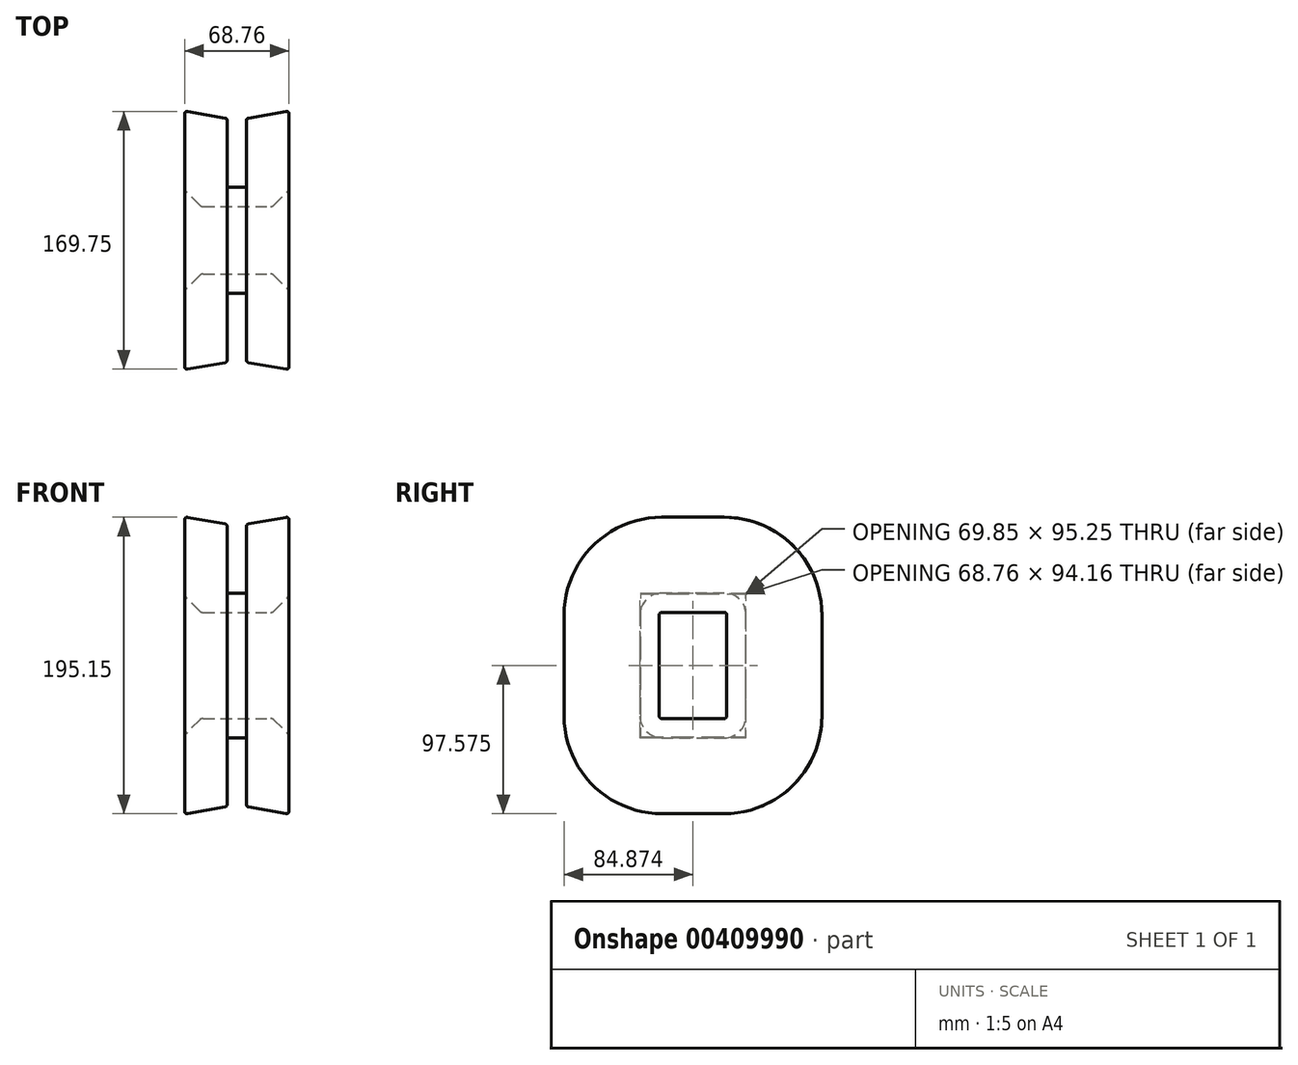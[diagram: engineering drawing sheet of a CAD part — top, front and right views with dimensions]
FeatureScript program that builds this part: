
annotation { "Feature Type Name" : "Feature", "Feature Type Description" : "" }
export const myFeature = defineFeature(function(context is Context, id is Id, definition is map)
    precondition{}
    {
        {
            var Q0;
            Q0=qCreatedBy(makeId("Top.planeOp"),FACE);
            var sketch = newSketch(context, id + "F0", { "sketchPlane" : qUnion([Q0])});
            skLineSegment(sketch, "E0", {"start": v(14, -36.1) * mm, "end": v(22.98, -27.12) * mm});
            skPoint(sketch, "E1.visualSharp", {"position": v(23.9, -26.2) * mm});
            skArc(sketch, "E1.filletArc", {"start": v(22.98, -27.12) * mm, "mid": v(23.66, -26.1) * mm, "end": v(23.9, -24.88) * mm});
            skPoint(sketch, "E2.visualSharp", {"position": v(13.07, -37.03) * mm});
            skArc(sketch, "E2.filletArc", {"start": v(11.75, -37.03) * mm, "mid": v(12.97, -36.79) * mm, "end": v(14, -36.1) * mm});
            skArc(sketch, "E3.MirrorCS", {"start": v(-32.7, -37.03) * mm, "mid": v(-33.91, -36.79) * mm, "end": v(-34.94, -36.1) * mm});
            skArc(sketch, "E4.MirrorCS", {"start": v(-43.92, -27.12) * mm, "mid": v(-44.61, -26.1) * mm, "end": v(-44.85, -24.88) * mm});
            skLineSegment(sketch, "E5.MirrorCS", {"start": v(-34.94, -36.1) * mm, "end": v(-43.92, -27.12) * mm});
            skPoint(sketch, "E6.visualSharp", {"position": v(31.35, 29.64) * mm});
            skLineSegment(sketch, "E7", {"start": v(-44.85, -24.88) * mm, "end": v(-44.85, 24.02) * mm});
            skLineSegment(sketch, "E8", {"start": v(-42.98, 25.6) * mm, "end": v(-18.15, 21.22) * mm});
            skLineSegment(sketch, "E9", {"start": v(-32.7, -37.03) * mm, "end": v(11.75, -37.03) * mm});
            skPoint(sketch, "E10.visualSharp", {"position": v(-44.85, 25.92) * mm});
            skArc(sketch, "E10.filletArc", {"start": v(-42.98, 25.6) * mm, "mid": v(-44.28, 25.24) * mm, "end": v(-44.85, 24.02) * mm});
            skArc(sketch, "E11.MirrorCS", {"start": v(22.03, 25.6) * mm, "mid": v(23.33, 25.24) * mm, "end": v(23.9, 24.02) * mm});
            skLineSegment(sketch, "E12.MirrorCS", {"start": v(23.9, -24.88) * mm, "end": v(23.9, 24.02) * mm});
            skLineSegment(sketch, "E13.MirrorCS", {"start": v(22.03, 25.6) * mm, "end": v(-2.8, 21.22) * mm});
            skPoint(sketch, "E14.MirrorP", {"position": v(31.35, 25.92) * mm});
            skLineSegment(sketch, "E15", {"start": v(-10.47, -24.33) * mm, "end": v(-16.82, -24.33) * mm});
            skLineSegment(sketch, "E16", {"start": v(-10.47, -24.33) * mm, "end": v(-4.12, -24.33) * mm});
            skLineSegment(sketch, "E17", {"start": v(-4.12, -24.33) * mm, "end": v(-4.12, 19.64) * mm});
            skLineSegment(sketch, "E18", {"start": v(-16.82, -24.33) * mm, "end": v(-16.82, 19.64) * mm});
            skArc(sketch, "E19.filletArc", {"start": v(-16.82, 19.64) * mm, "mid": v(-17.2, 20.67) * mm, "end": v(-18.15, 21.22) * mm});
            skArc(sketch, "E20.filletArc", {"start": v(-2.8, 21.22) * mm, "mid": v(-3.75, 20.67) * mm, "end": v(-4.12, 19.64) * mm});
            skSolve(sketch);
        }
        {
            var Q0;
            Q0=qCreatedBy(makeId("Right.planeOp"),FACE);
            var sketch = newSketch(context, id + "F1", { "sketchPlane" : qUnion([Q0])});
            skLineSegment(sketch, "E21", {"start": v(-37.03, 0) * mm, "end": v(-37.03, 30.15) * mm});
            skLineSegment(sketch, "E22", {"start": v(-38.63, 31.75) * mm, "end": v(-79.88, 31.75) * mm});
            skLineSegment(sketch, "E23", {"start": v(-81.48, 30.15) * mm, "end": v(-81.48, -3.18) * mm});
            skPoint(sketch, "E24.visualSharp", {"position": v(-37.03, 31.75) * mm});
            skArc(sketch, "E24.filletArc", {"start": v(-37.03, 30.15) * mm, "mid": v(-37.5, 31.28) * mm, "end": v(-38.63, 31.75) * mm});
            skPoint(sketch, "E25.visualSharp", {"position": v(-81.48, 31.75) * mm});
            skArc(sketch, "E25.filletArc", {"start": v(-79.88, 31.75) * mm, "mid": v(-81.01, 31.28) * mm, "end": v(-81.48, 30.15) * mm});
            skLineSegment(sketch, "E26", {"start": v(-81.48, -3.18) * mm, "end": v(-128.97, -3.18) * mm});
            skArc(sketch, "E27.MirrorCS", {"start": v(-37.03, -36.5) * mm, "mid": v(-37.5, -37.63) * mm, "end": v(-38.63, -38.1) * mm});
            skPoint(sketch, "E28.MirrorP", {"position": v(-37.03, -38.1) * mm});
            skPoint(sketch, "E29.MirrorP", {"position": v(-81.48, -38.1) * mm});
            skLineSegment(sketch, "E30.MirrorCS", {"start": v(-81.48, -36.5) * mm, "end": v(-81.48, -3.18) * mm});
            skArc(sketch, "E31.MirrorCS", {"start": v(-79.88, -38.1) * mm, "mid": v(-81.01, -37.63) * mm, "end": v(-81.48, -36.5) * mm});
            skLineSegment(sketch, "E32.MirrorCS", {"start": v(-38.63, -38.1) * mm, "end": v(-59.26, -38.1) * mm});
            skLineSegment(sketch, "E33.MirrorCS", {"start": v(-37.03, -6.35) * mm, "end": v(-37.03, -36.5) * mm});
            skLineSegment(sketch, "E34", {"start": v(-59.26, -38.1) * mm, "end": v(-79.88, -38.1) * mm});
            skLineSegment(sketch, "E35", {"start": v(-37.03, 0) * mm, "end": v(-37.03, -6.35) * mm});
            skSolve(sketch);
        }
        {
            var Q0;
            Q0=makeQuery(id+"F0.imprint","IMPRINT",FACE,{"disambiguationData":[TD([[makeQuery(id+"F0.imprint","IMPRINT",EDGE,{"derivedFrom":sQuery(id+"F0.wireOp",EDGE,"E0")}),1.0]])]});
            var Q1;
            Q1=sQuery(id+"F1.wireOp",EDGE,"E21");
            var Q2;
            Q2=sQuery(id+"F1.wireOp",EDGE,"E24.filletArc");
            var Q3;
            Q3=sQuery(id+"F1.wireOp",EDGE,"E22");
            var Q4;
            Q4=sQuery(id+"F1.wireOp",EDGE,"E25.filletArc");
            var Q5;
            Q5=sQuery(id+"F1.wireOp",EDGE,"E23");
            var Q6;
            Q6=sQuery(id+"F1.wireOp",EDGE,"E30.MirrorCS");
            var Q7;
            Q7=sQuery(id+"F1.wireOp",EDGE,"E31.MirrorCS");
            var Q8;
            Q8=sQuery(id+"F1.wireOp",EDGE,"E34");
            var Q9;
            Q9=sQuery(id+"F1.wireOp",EDGE,"E32.MirrorCS");
            var Q10;
            Q10=sQuery(id+"F1.wireOp",EDGE,"E27.MirrorCS");
            var Q11;
            Q11=sQuery(id+"F1.wireOp",EDGE,"E33.MirrorCS");
            var Q12;
            Q12=sQuery(id+"F1.wireOp",EDGE,"E35");
            sweep(context, id + "F2", {"profiles" : qUnion([Q0]), "path" : qUnion([Q1, Q2, Q3, Q4, Q5, Q6, Q7, Q8, Q9, Q10, Q11, Q12])});
        }
    });
